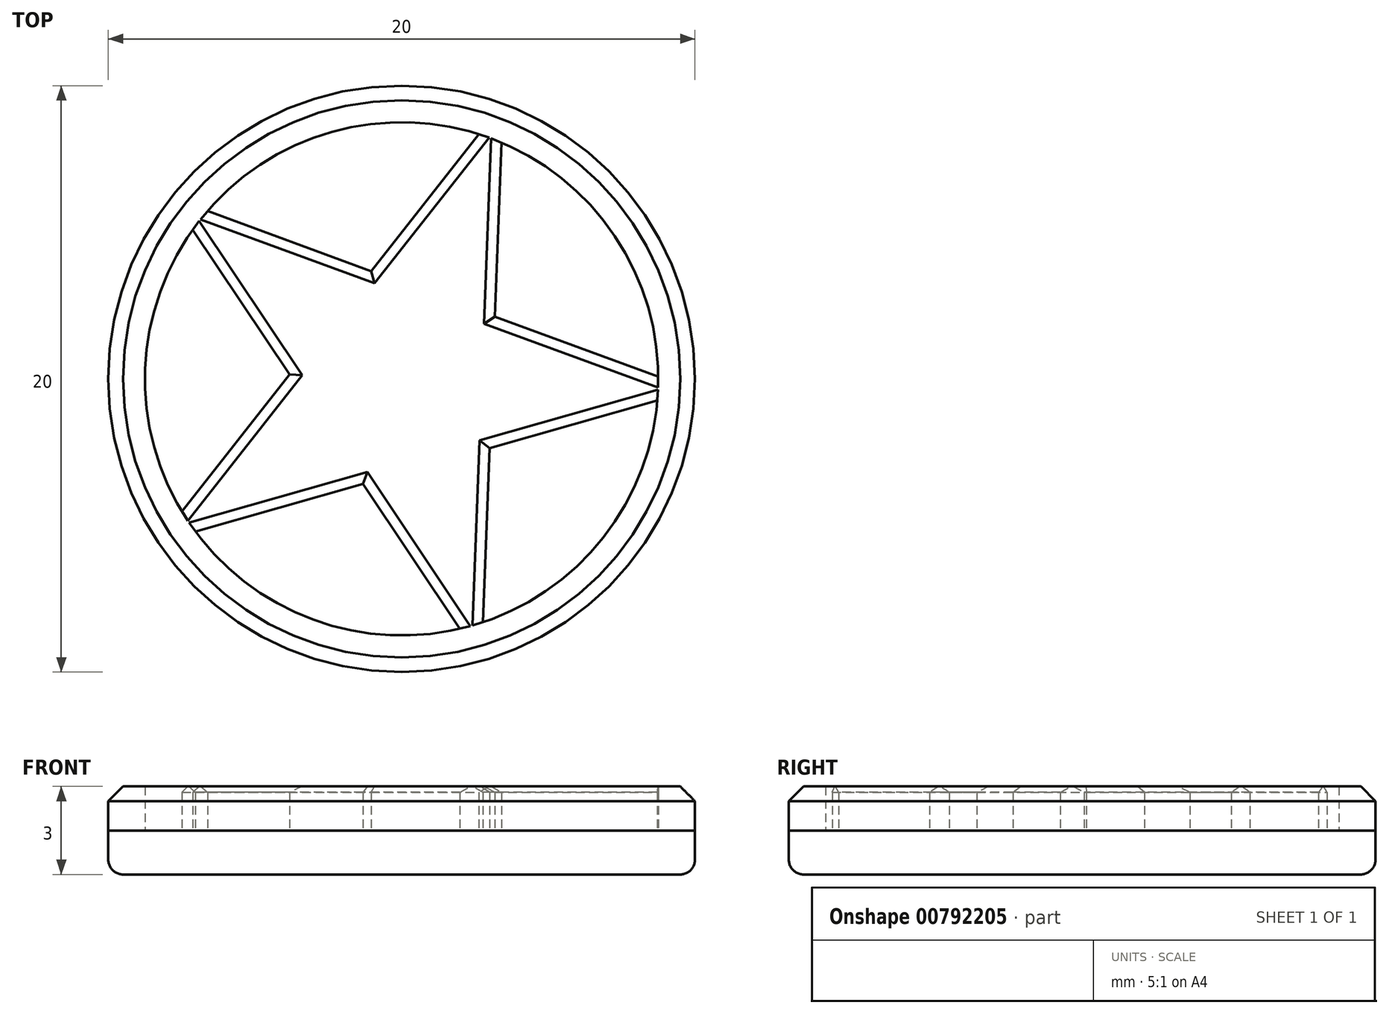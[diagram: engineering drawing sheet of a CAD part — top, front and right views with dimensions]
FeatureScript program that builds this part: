
annotation { "Feature Type Name" : "Feature", "Feature Type Description" : "" }
export const myFeature = defineFeature(function(context is Context, id is Id, definition is map)
    precondition{}
    {
        {
            assignVariable(context, id + "F0", {"name" : "height", "anyValue" : 3 * mm});
        }
        {
            assignVariable(context, id + "F1", {"name" : "relief", "anyValue" : getVariable(context, 'height') / 2});
        }
        {
            var Q0;
            Q0=qCreatedBy(makeId("Top.planeOp"),FACE);
            var sketch = newSketch(context, id + "F2", { "sketchPlane" : qUnion([Q0])});
            skCircle(sketch, "E0", {"center": v(0, 0) * mm, "radius": 10 * mm});
            skSolve(sketch);
        }
        {
            var Q0;
            Q0=makeQuery(id+"F2.imprint","IMPRINT",FACE,{"disambiguationData":[TD([[makeQuery(id+"F2.imprint","IMPRINT",EDGE,{"derivedFrom":sQuery(id+"F2.wireOp",EDGE,"E0")}),1.0]])]});
            extrude(context, id + "F3", {"entities" : qUnion([Q0]), "depth" : getVariable(context, 'height') / 2, "offsetDistance" : 25 * mm});
        }
        {
            var Q0;
            Q0=makeQuery(id+"F3.opExtrude","CAP_FACE",FACE,{"disambiguationData":[OSD([sQuery(id+"F2.wireOp",EDGE,"E0")])],"isStart":false});
            var sketch = newSketch(context, id + "F4", { "sketchPlane" : qUnion([Q0])});
            skCircle(sketch, "E1", {"center": v(0, 0) * mm, "radius": 10 * mm});
            skCircle(sketch, "E2", {"center": v(0, 0) * mm, "radius": 8.75 * mm});
            skCircle(sketch, "E3.cCircle", {"center": v(0, 0) * mm, "radius": 10 * mm, "construction": true});
            skLineSegment(sketch, "E3.0", {"start": v(3.45, 9.39) * mm, "end": v(10, -0.38) * mm, "construction": true});
            skLineSegment(sketch, "E3.1", {"start": v(10, -0.38) * mm, "end": v(2.72, -9.62) * mm, "construction": true});
            skLineSegment(sketch, "E3.2", {"start": v(2.72, -9.62) * mm, "end": v(-8.3, -5.56) * mm, "construction": true});
            skLineSegment(sketch, "E3.3", {"start": v(-8.3, -5.56) * mm, "end": v(-7.86, 6.18) * mm, "construction": true});
            skLineSegment(sketch, "E3.4", {"start": v(-7.86, 6.18) * mm, "end": v(3.45, 9.39) * mm, "construction": true});
            skLineSegment(sketch, "E4", {"start": v(-7.86, 6.18) * mm, "end": v(2.72, -9.62) * mm});
            skLineSegment(sketch, "E5", {"start": v(3.45, 9.39) * mm, "end": v(2.72, -9.62) * mm});
            skLineSegment(sketch, "E6", {"start": v(-8.3, -5.56) * mm, "end": v(10, -0.38) * mm});
            skLineSegment(sketch, "E7", {"start": v(10, -0.38) * mm, "end": v(-7.86, 6.18) * mm});
            skLineSegment(sketch, "E8", {"start": v(3.45, 9.39) * mm, "end": v(-8.3, -5.56) * mm});
            skSolve(sketch);
        }
        {
            var Q0;
            {var subQ0=sQuery(id+"F4.wireOp",EDGE,"E5");var subQ1=sQuery(id+"F4.wireOp",EDGE,"E2");var subQ2=makeQuery(id+"F4.imprint","INTERSECT",VERTEX,{"disambiguationData":[OD(0.0)],"derivedFrom":[subQ1,subQ0]});Q0=makeQuery(id+"F4.imprint","IMPRINT",FACE,{"disambiguationData":[TD([[makeQuery(id+"F4.imprint","IMPRINT",EDGE,{"disambiguationData":[TD([[subQ2,-1.0]])],"derivedFrom":subQ1}),1.0]])]});}
            var Q1;
            {var subQ0=sQuery(id+"F4.wireOp",EDGE,"E5");var subQ5=sQuery(id+"F4.wireOp",EDGE,"E2");var subQ6=makeQuery(id+"F4.imprint","INTERSECT",VERTEX,{"disambiguationData":[OD(0.0)],"derivedFrom":[subQ5,subQ0]});Q1=makeQuery(id+"F4.imprint","IMPRINT",FACE,{"disambiguationData":[TD([[makeQuery(id+"F4.imprint","IMPRINT",EDGE,{"disambiguationData":[TD([[subQ6,1.0]])],"derivedFrom":subQ5}),-1.0]])]});}
            var Q2;
            {var subQ3=sQuery(id+"F4.wireOp",EDGE,"E8");var subQ5=sQuery(id+"F4.wireOp",EDGE,"E2");var subQ6=makeQuery(id+"F4.imprint","INTERSECT",VERTEX,{"disambiguationData":[OD(0.0)],"derivedFrom":[subQ5,subQ3]});Q2=makeQuery(id+"F4.imprint","IMPRINT",FACE,{"disambiguationData":[TD([[makeQuery(id+"F4.imprint","IMPRINT",EDGE,{"disambiguationData":[TD([[subQ6,-1.0]])],"derivedFrom":subQ5}),-1.0]])]});}
            var Q3;
            {var subQ0=sQuery(id+"F4.wireOp",EDGE,"E8");var subQ1=sQuery(id+"F4.wireOp",EDGE,"E2");var subQ2=makeQuery(id+"F4.imprint","INTERSECT",VERTEX,{"disambiguationData":[OD(1.0)],"derivedFrom":[subQ1,subQ0]});Q3=makeQuery(id+"F4.imprint","IMPRINT",FACE,{"disambiguationData":[TD([[makeQuery(id+"F4.imprint","IMPRINT",EDGE,{"disambiguationData":[TD([[subQ2,-1.0]])],"derivedFrom":subQ1}),1.0]])]});}
            var Q4;
            {var subQ0=sQuery(id+"F4.wireOp",EDGE,"E4");var subQ1=sQuery(id+"F4.wireOp",EDGE,"E2");var subQ2=makeQuery(id+"F4.imprint","INTERSECT",VERTEX,{"disambiguationData":[OD(1.0)],"derivedFrom":[subQ1,subQ0]});Q4=makeQuery(id+"F4.imprint","IMPRINT",FACE,{"disambiguationData":[TD([[makeQuery(id+"F4.imprint","IMPRINT",EDGE,{"disambiguationData":[TD([[subQ2,-1.0]])],"derivedFrom":subQ1}),1.0]])]});}
            var Q5;
            {var subQ0=sQuery(id+"F4.wireOp",EDGE,"E7");var subQ1=sQuery(id+"F4.wireOp",EDGE,"E2");var subQ2=makeQuery(id+"F4.imprint","INTERSECT",VERTEX,{"disambiguationData":[OD(0.0)],"derivedFrom":[subQ1,subQ0]});Q5=makeQuery(id+"F4.imprint","IMPRINT",FACE,{"disambiguationData":[TD([[makeQuery(id+"F4.imprint","IMPRINT",EDGE,{"disambiguationData":[TD([[subQ2,1.0]])],"derivedFrom":subQ1}),-1.0]])]});}
            var Q6;
            {var subQ0=sQuery(id+"F4.wireOp",EDGE,"E5");var subQ5=sQuery(id+"F4.wireOp",EDGE,"E2");var subQ6=makeQuery(id+"F4.imprint","INTERSECT",VERTEX,{"disambiguationData":[OD(1.0)],"derivedFrom":[subQ5,subQ0]});Q6=makeQuery(id+"F4.imprint","IMPRINT",FACE,{"disambiguationData":[TD([[makeQuery(id+"F4.imprint","IMPRINT",EDGE,{"disambiguationData":[TD([[subQ6,-1.0]])],"derivedFrom":subQ5}),-1.0]])]});}
            var Q7;
            {var subQ0=sQuery(id+"F4.wireOp",EDGE,"E4");var subQ1=sQuery(id+"F4.wireOp",EDGE,"E2");var subQ2=makeQuery(id+"F4.imprint","INTERSECT",VERTEX,{"disambiguationData":[OD(1.0)],"derivedFrom":[subQ1,subQ0]});Q7=makeQuery(id+"F4.imprint","IMPRINT",FACE,{"disambiguationData":[TD([[makeQuery(id+"F4.imprint","IMPRINT",EDGE,{"disambiguationData":[TD([[subQ2,-1.0]])],"derivedFrom":subQ1}),-1.0]])]});}
            var Q8;
            {var subQ3=sQuery(id+"F4.wireOp",EDGE,"E6");var subQ5=sQuery(id+"F4.wireOp",EDGE,"E2");var subQ6=makeQuery(id+"F4.imprint","INTERSECT",VERTEX,{"disambiguationData":[OD(0.0)],"derivedFrom":[subQ5,subQ3]});Q8=makeQuery(id+"F4.imprint","IMPRINT",FACE,{"disambiguationData":[TD([[makeQuery(id+"F4.imprint","IMPRINT",EDGE,{"disambiguationData":[TD([[subQ6,-1.0]])],"derivedFrom":subQ5}),-1.0]])]});}
            var Q9;
            {var subQ0=sQuery(id+"F4.wireOp",EDGE,"E7");var subQ1=sQuery(id+"F4.wireOp",EDGE,"E2");var subQ2=makeQuery(id+"F4.imprint","INTERSECT",VERTEX,{"disambiguationData":[OD(1.0)],"derivedFrom":[subQ1,subQ0]});Q9=makeQuery(id+"F4.imprint","IMPRINT",FACE,{"disambiguationData":[TD([[makeQuery(id+"F4.imprint","IMPRINT",EDGE,{"disambiguationData":[TD([[subQ2,-1.0]])],"derivedFrom":subQ1}),-1.0]])]});}
            var Q10;
            {var subQ3=sQuery(id+"F4.wireOp",EDGE,"E8");var subQ6=sQuery(id+"F4.wireOp",EDGE,"E4");var subQ9=makeQuery(id+"F4.imprint","INTERSECT",VERTEX,{"derivedFrom":[subQ6,subQ3]});Q10=makeQuery(id+"F4.imprint","IMPRINT",FACE,{"disambiguationData":[TD([[makeQuery(id+"F4.imprint","IMPRINT",EDGE,{"disambiguationData":[TD([[subQ9,-1.0]])],"derivedFrom":subQ6}),1.0]])]});}
            var Q11;
            {var subQ0=sQuery(id+"F4.wireOp",EDGE,"E8");var subQ1=sQuery(id+"F4.wireOp",EDGE,"E2");var subQ2=makeQuery(id+"F4.imprint","INTERSECT",VERTEX,{"disambiguationData":[OD(1.0)],"derivedFrom":[subQ1,subQ0]});Q11=makeQuery(id+"F4.imprint","IMPRINT",FACE,{"disambiguationData":[TD([[makeQuery(id+"F4.imprint","IMPRINT",EDGE,{"disambiguationData":[TD([[subQ2,-1.0]])],"derivedFrom":subQ1}),-1.0]])]});}
            var Q12;
            {var subQ0=sQuery(id+"F4.wireOp",EDGE,"E4");var subQ5=sQuery(id+"F4.wireOp",EDGE,"E2");var subQ6=makeQuery(id+"F4.imprint","INTERSECT",VERTEX,{"disambiguationData":[OD(0.0)],"derivedFrom":[subQ5,subQ0]});Q12=makeQuery(id+"F4.imprint","IMPRINT",FACE,{"disambiguationData":[TD([[makeQuery(id+"F4.imprint","IMPRINT",EDGE,{"disambiguationData":[TD([[subQ6,-1.0]])],"derivedFrom":subQ5}),-1.0]])]});}
            var Q13;
            {var subQ0=sQuery(id+"F4.wireOp",EDGE,"E5");var subQ1=sQuery(id+"F4.wireOp",EDGE,"E2");var subQ2=makeQuery(id+"F4.imprint","INTERSECT",VERTEX,{"disambiguationData":[OD(0.0)],"derivedFrom":[subQ1,subQ0]});Q13=makeQuery(id+"F4.imprint","IMPRINT",FACE,{"disambiguationData":[TD([[makeQuery(id+"F4.imprint","IMPRINT",EDGE,{"disambiguationData":[TD([[subQ2,-1.0]])],"derivedFrom":subQ1}),-1.0]])]});}
            var Q14;
            {var subQ0=sQuery(id+"F4.wireOp",EDGE,"E6");var subQ1=sQuery(id+"F4.wireOp",EDGE,"E2");var subQ2=makeQuery(id+"F4.imprint","INTERSECT",VERTEX,{"disambiguationData":[OD(1.0)],"derivedFrom":[subQ1,subQ0]});Q14=makeQuery(id+"F4.imprint","IMPRINT",FACE,{"disambiguationData":[TD([[makeQuery(id+"F4.imprint","IMPRINT",EDGE,{"disambiguationData":[TD([[subQ2,-1.0]])],"derivedFrom":subQ1}),1.0]])]});}
            var Q15;
            {var subQ0=sQuery(id+"F4.wireOp",EDGE,"E6");var subQ1=sQuery(id+"F4.wireOp",EDGE,"E2");var subQ2=makeQuery(id+"F4.imprint","INTERSECT",VERTEX,{"disambiguationData":[OD(1.0)],"derivedFrom":[subQ1,subQ0]});Q15=makeQuery(id+"F4.imprint","IMPRINT",FACE,{"disambiguationData":[TD([[makeQuery(id+"F4.imprint","IMPRINT",EDGE,{"disambiguationData":[TD([[subQ2,-1.0]])],"derivedFrom":subQ1}),-1.0]])]});}
            var Q16;
            {var subQ0=sQuery(id+"F4.wireOp",EDGE,"E7");var subQ1=sQuery(id+"F4.wireOp",EDGE,"E2");var subQ2=makeQuery(id+"F4.imprint","INTERSECT",VERTEX,{"disambiguationData":[OD(0.0)],"derivedFrom":[subQ1,subQ0]});Q16=makeQuery(id+"F4.imprint","IMPRINT",FACE,{"disambiguationData":[TD([[makeQuery(id+"F4.imprint","IMPRINT",EDGE,{"disambiguationData":[TD([[subQ2,-1.0]])],"derivedFrom":subQ1}),-1.0]])]});}
            var Q17;
            {var subQ0=sQuery(id+"F4.wireOp",EDGE,"E7");var subQ1=sQuery(id+"F4.wireOp",EDGE,"E2");var subQ2=makeQuery(id+"F4.imprint","INTERSECT",VERTEX,{"disambiguationData":[OD(1.0)],"derivedFrom":[subQ1,subQ0]});Q17=makeQuery(id+"F4.imprint","IMPRINT",FACE,{"disambiguationData":[TD([[makeQuery(id+"F4.imprint","IMPRINT",EDGE,{"disambiguationData":[TD([[subQ2,-1.0]])],"derivedFrom":subQ1}),1.0]])]});}
            extrude(context, id + "F5", {"entities" : qUnion([Q0, Q1, Q2, Q3, Q4, Q5, Q6, Q7, Q8, Q9, Q10, Q11, Q12, Q13, Q14, Q15, Q16, Q17]), "depth" : getVariable(context, 'relief'), "offsetDistance" : 25 * mm});
        }
        {
            var Q0;
            Q0=makeQuery(id+"F5.opExtrude","CAP_FACE",FACE,{"disambiguationData":[OSD([sQuery(id+"F4.wireOp",EDGE,"E1"),sQuery(id+"F4.wireOp",EDGE,"E2"),sQuery(id+"F4.wireOp",EDGE,"E4"),sQuery(id+"F4.wireOp",EDGE,"E5"),sQuery(id+"F4.wireOp",EDGE,"E6"),sQuery(id+"F4.wireOp",EDGE,"E7"),sQuery(id+"F4.wireOp",EDGE,"E8")])],"isStart":false});
            var Q1;
            Q1=makeQuery(id+"F3.opExtrude","CAP_FACE",FACE,{"disambiguationData":[OSD([sQuery(id+"F2.wireOp",EDGE,"E0")])],"isStart":true});
            fillet(context, id + "F6", {"entities" : qUnion([Q0, Q1]), "radius" : 0.5 * mm, "tangentPropagation" : true, "allowEdgeOverflow" : false});
        }
        {
            var Q0;
            {var subQ0=sQuery(id+"F4.wireOp",EDGE,"E7");Q0=makeQuery(id+"F5.opExtrude","CAP_EDGE",EDGE,{"disambiguationData":[OSD([subQ0]),TDD([makeQuery(id+"F4.imprint","IMPRINT",EDGE,{"disambiguationData":[TD([[makeQuery(id+"F4.imprint","INTERSECT",VERTEX,{"disambiguationData":[OD(0.0)],"derivedFrom":[sQuery(id+"F4.wireOp",EDGE,"E2"),subQ0]}),1.0]])],"derivedFrom":subQ0})])],"isStart":false});}
            var Q1;
            {var subQ0=sQuery(id+"F4.wireOp",EDGE,"E8");Q1=makeQuery(id+"F5.opExtrude","CAP_EDGE",EDGE,{"disambiguationData":[OSD([subQ0]),TDD([makeQuery(id+"F4.imprint","IMPRINT",EDGE,{"disambiguationData":[TD([[makeQuery(id+"F4.imprint","INTERSECT",VERTEX,{"disambiguationData":[OD(0.0)],"derivedFrom":[sQuery(id+"F4.wireOp",EDGE,"E2"),subQ0]}),-1.0]])],"derivedFrom":subQ0})])],"isStart":false});}
            var Q2;
            {var subQ0=sQuery(id+"F4.wireOp",EDGE,"E5");Q2=makeQuery(id+"F5.opExtrude","CAP_EDGE",EDGE,{"disambiguationData":[OSD([subQ0]),TDD([makeQuery(id+"F4.imprint","IMPRINT",EDGE,{"disambiguationData":[TD([[makeQuery(id+"F4.imprint","INTERSECT",VERTEX,{"disambiguationData":[OD(0.0)],"derivedFrom":[sQuery(id+"F4.wireOp",EDGE,"E2"),subQ0]}),-1.0]])],"derivedFrom":subQ0})])],"isStart":false});}
            var Q3;
            {var subQ0=sQuery(id+"F4.wireOp",EDGE,"E7");Q3=makeQuery(id+"F5.opExtrude","CAP_EDGE",EDGE,{"disambiguationData":[OSD([subQ0]),TDD([makeQuery(id+"F4.imprint","IMPRINT",EDGE,{"disambiguationData":[TD([[makeQuery(id+"F4.imprint","INTERSECT",VERTEX,{"disambiguationData":[OD(1.0)],"derivedFrom":[sQuery(id+"F4.wireOp",EDGE,"E2"),subQ0]}),-1.0]])],"derivedFrom":subQ0})])],"isStart":false});}
            var Q4;
            {var subQ0=sQuery(id+"F4.wireOp",EDGE,"E6");Q4=makeQuery(id+"F5.opExtrude","CAP_EDGE",EDGE,{"disambiguationData":[OSD([subQ0]),TDD([makeQuery(id+"F4.imprint","IMPRINT",EDGE,{"disambiguationData":[TD([[makeQuery(id+"F4.imprint","INTERSECT",VERTEX,{"disambiguationData":[OD(1.0)],"derivedFrom":[sQuery(id+"F4.wireOp",EDGE,"E2"),subQ0]}),1.0]])],"derivedFrom":subQ0})])],"isStart":false});}
            var Q5;
            {var subQ0=sQuery(id+"F4.wireOp",EDGE,"E5");Q5=makeQuery(id+"F5.opExtrude","CAP_EDGE",EDGE,{"disambiguationData":[OSD([subQ0]),TDD([makeQuery(id+"F4.imprint","IMPRINT",EDGE,{"disambiguationData":[TD([[makeQuery(id+"F4.imprint","INTERSECT",VERTEX,{"disambiguationData":[OD(1.0)],"derivedFrom":[sQuery(id+"F4.wireOp",EDGE,"E2"),subQ0]}),1.0]])],"derivedFrom":subQ0})])],"isStart":false});}
            var Q6;
            {var subQ0=sQuery(id+"F4.wireOp",EDGE,"E4");Q6=makeQuery(id+"F5.opExtrude","CAP_EDGE",EDGE,{"disambiguationData":[OSD([subQ0]),TDD([makeQuery(id+"F4.imprint","IMPRINT",EDGE,{"disambiguationData":[TD([[makeQuery(id+"F4.imprint","INTERSECT",VERTEX,{"disambiguationData":[OD(1.0)],"derivedFrom":[sQuery(id+"F4.wireOp",EDGE,"E2"),subQ0]}),1.0]])],"derivedFrom":subQ0})])],"isStart":false});}
            var Q7;
            {var subQ0=sQuery(id+"F4.wireOp",EDGE,"E6");Q7=makeQuery(id+"F5.opExtrude","CAP_EDGE",EDGE,{"disambiguationData":[OSD([subQ0]),TDD([makeQuery(id+"F4.imprint","IMPRINT",EDGE,{"disambiguationData":[TD([[makeQuery(id+"F4.imprint","INTERSECT",VERTEX,{"disambiguationData":[OD(0.0)],"derivedFrom":[sQuery(id+"F4.wireOp",EDGE,"E2"),subQ0]}),-1.0]])],"derivedFrom":subQ0})])],"isStart":false});}
            var Q8;
            {var subQ0=sQuery(id+"F4.wireOp",EDGE,"E8");Q8=makeQuery(id+"F5.opExtrude","CAP_EDGE",EDGE,{"disambiguationData":[OSD([subQ0]),TDD([makeQuery(id+"F4.imprint","IMPRINT",EDGE,{"disambiguationData":[TD([[makeQuery(id+"F4.imprint","INTERSECT",VERTEX,{"disambiguationData":[OD(1.0)],"derivedFrom":[sQuery(id+"F4.wireOp",EDGE,"E2"),subQ0]}),1.0]])],"derivedFrom":subQ0})])],"isStart":false});}
            var Q9;
            {var subQ0=sQuery(id+"F4.wireOp",EDGE,"E4");Q9=makeQuery(id+"F5.opExtrude","CAP_EDGE",EDGE,{"disambiguationData":[OSD([subQ0]),TDD([makeQuery(id+"F4.imprint","IMPRINT",EDGE,{"disambiguationData":[TD([[makeQuery(id+"F4.imprint","INTERSECT",VERTEX,{"disambiguationData":[OD(0.0)],"derivedFrom":[sQuery(id+"F4.wireOp",EDGE,"E2"),subQ0]}),-1.0]])],"derivedFrom":subQ0})])],"isStart":false});}
            var Q10;
            {var subQ0=sQuery(id+"F4.wireOp",EDGE,"E7");Q10=makeQuery(id+"F5.opExtrude","CAP_EDGE",EDGE,{"disambiguationData":[OSD([subQ0]),TDD([makeQuery(id+"F4.imprint","IMPRINT",EDGE,{"disambiguationData":[TD([[makeQuery(id+"F4.imprint","INTERSECT",VERTEX,{"disambiguationData":[OD(0.0)],"derivedFrom":[sQuery(id+"F4.wireOp",EDGE,"E2"),subQ0]}),-1.0]])],"derivedFrom":subQ0})])],"isStart":false});}
            var Q11;
            {var subQ0=sQuery(id+"F4.wireOp",EDGE,"E7");Q11=makeQuery(id+"F5.opExtrude","CAP_EDGE",EDGE,{"disambiguationData":[OSD([subQ0]),TDD([makeQuery(id+"F4.imprint","IMPRINT",EDGE,{"disambiguationData":[TD([[makeQuery(id+"F4.imprint","INTERSECT",VERTEX,{"disambiguationData":[OD(1.0)],"derivedFrom":[sQuery(id+"F4.wireOp",EDGE,"E2"),subQ0]}),1.0]])],"derivedFrom":subQ0})])],"isStart":false});}
            chamfer(context, id + "F7", {"entities" : qUnion([Q0, Q1, Q2, Q3, Q4, Q5, Q6, Q7, Q8, Q9, Q10, Q11]), "chamferType" : ChamferType.OFFSET_ANGLE, "width" : 0.35 * mm, "oppositeDirection" : false, "angle" : 30 * degree, "tangentPropagation" : true});
        }
        {
            var Q0;
            Q0=makeQuery(id+"F5.opExtrude","CAP_EDGE",EDGE,{"disambiguationData":[OSD([sQuery(id+"F4.wireOp",EDGE,"E1")])],"isStart":false});
            var Q1;
            Q1=makeQuery(id+"F3.opExtrude","CAP_EDGE",EDGE,{"disambiguationData":[OSD([sQuery(id+"F2.wireOp",EDGE,"E0")])],"isStart":true});
            chamfer(context, id + "F8", {"entities" : qUnion([Q0, Q1]), "width" : 0.5 * mm, "tangentPropagation" : true});
        }
    });
